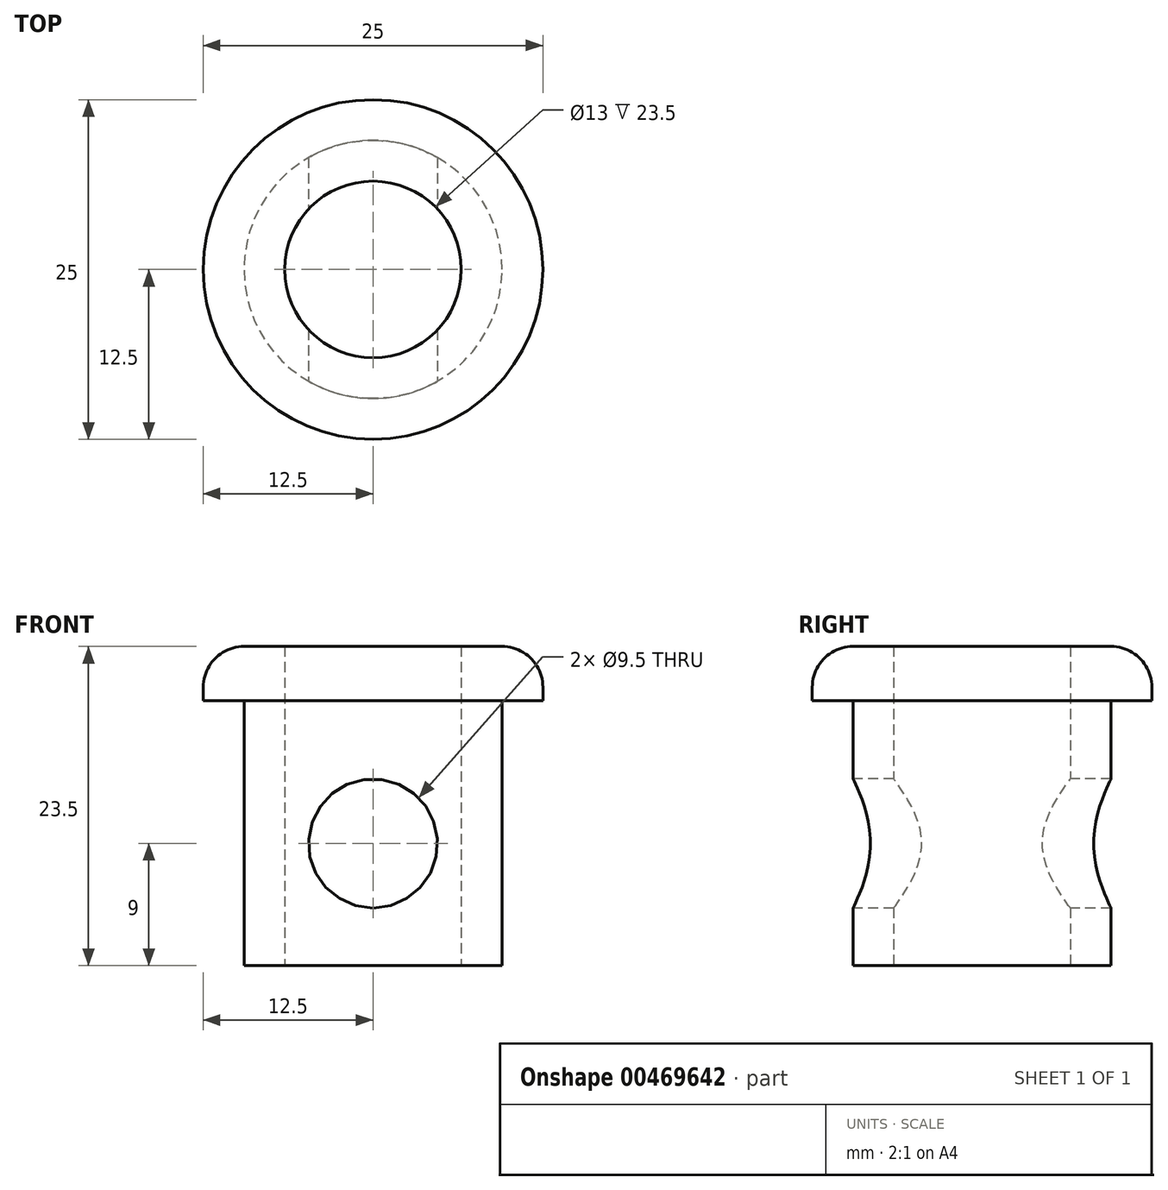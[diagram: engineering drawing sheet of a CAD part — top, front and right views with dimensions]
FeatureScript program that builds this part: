
annotation { "Feature Type Name" : "Feature", "Feature Type Description" : "" }
export const myFeature = defineFeature(function(context is Context, id is Id, definition is map)
    precondition{}
    {
        {
            var Q0;
            Q0=qCreatedBy(makeId("Top.planeOp"),FACE);
            var sketch = newSketch(context, id + "F0", { "sketchPlane" : qUnion([Q0])});
            skCircle(sketch, "E0", {"center": v(0, 0) * mm, "radius": 6.5 * mm});
            skCircle(sketch, "E1.0", {"center": v(0, 0) * mm, "radius": 9.5 * mm});
            skSolve(sketch);
        }
        {
            var Q0;
            Q0 = qSketchRegion(id + "F0", true);
            extrude(context, id + "F1", {"entities" : qUnion([Q0]), "depth" : 19.5 * mm});
        }
        {
            var Q0;
            Q0=makeQuery(id+"F1.opExtrude","CAP_FACE",FACE,{"disambiguationData":[OSD([sQuery(id+"F0.wireOp",EDGE,"E0"),sQuery(id+"F0.wireOp",EDGE,"E1.0")])],"isStart":false});
            var sketch = newSketch(context, id + "F2", { "sketchPlane" : qUnion([Q0])});
            skCircle(sketch, "E2.0", {"center": v(0, 0) * mm, "radius": 6.5 * mm});
            skCircle(sketch, "E3", {"center": v(0, 0) * mm, "radius": 12.5 * mm});
            skSolve(sketch);
        }
        {
            var Q0;
            Q0 = qSketchRegion(id + "F2", true);
            extrude(context, id + "F3", {"entities" : qUnion([Q0]), "operationType" : NewBodyOperationType.ADD, "depth" : 4 * mm});
        }
        {
            var Q0;
            Q0=makeQuery(id+"F3.opExtrude","CAP_EDGE",EDGE,{"disambiguationData":[OSD([sQuery(id+"F2.wireOp",EDGE,"E3")])],"isStart":false});
            fillet(context, id + "F4", {"entities" : qUnion([Q0]), "radius" : 3 * mm, "tangentPropagation" : true, "allowEdgeOverflow" : false});
        }
        {
            var Q0;
            Q0=qCreatedBy(makeId("Front.planeOp"),FACE);
            var sketch = newSketch(context, id + "F5", { "sketchPlane" : qUnion([Q0])});
            skCircle(sketch, "E4", {"center": v(0, 9) * mm, "radius": 4.75 * mm});
            skSolve(sketch);
        }
        {
            var Q0;
            Q0 = qSketchRegion(id + "F5", true);
            extrude(context, id + "F6", {"entities" : qUnion([Q0]), "operationType" : NewBodyOperationType.REMOVE, "oppositeDirection" : true, "depth" : 25 * mm, "hasSecondDirection" : true, "secondDirectionOppositeDirection" : false, "secondDirectionDepth" : 25 * mm});
        }
    });
